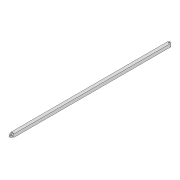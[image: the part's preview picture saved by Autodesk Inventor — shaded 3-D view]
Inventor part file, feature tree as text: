
AUTODESK INVENTOR PART (.ipt)
format: ipt  version: 2022 (Build 260153000, 153)  size: 94,720 bytes
history: native  units: mm
features: extrude x3, sketch x3
ambient origin geometry x8: Origin, YZ Plane, XZ Plane, XY Plane, X Axis, Y Axis, Z Axis, Center Point
bodies: Solid1 (feature_tree)
feature tree (6):
  extrude  "Extrusion1"  Depth=8.0mm
  extrude  "Extrusion2"  Depth=3.2mm
  extrude  "Extrusion3"  Depth=2.1mm
  sketch  "Sketch1"  dims[d0=411.151mm d1=8.0mm]
  sketch  "Sketch2"  dims[d2=3.2mm d3=3.2mm]
  sketch  "Sketch3"  dims[d4=8.0mm d5=0.0mm d6=1.0mm d7=2.1mm d8=0.0mm d9=1.0mm d10=2.1mm d11=0.0mm]
